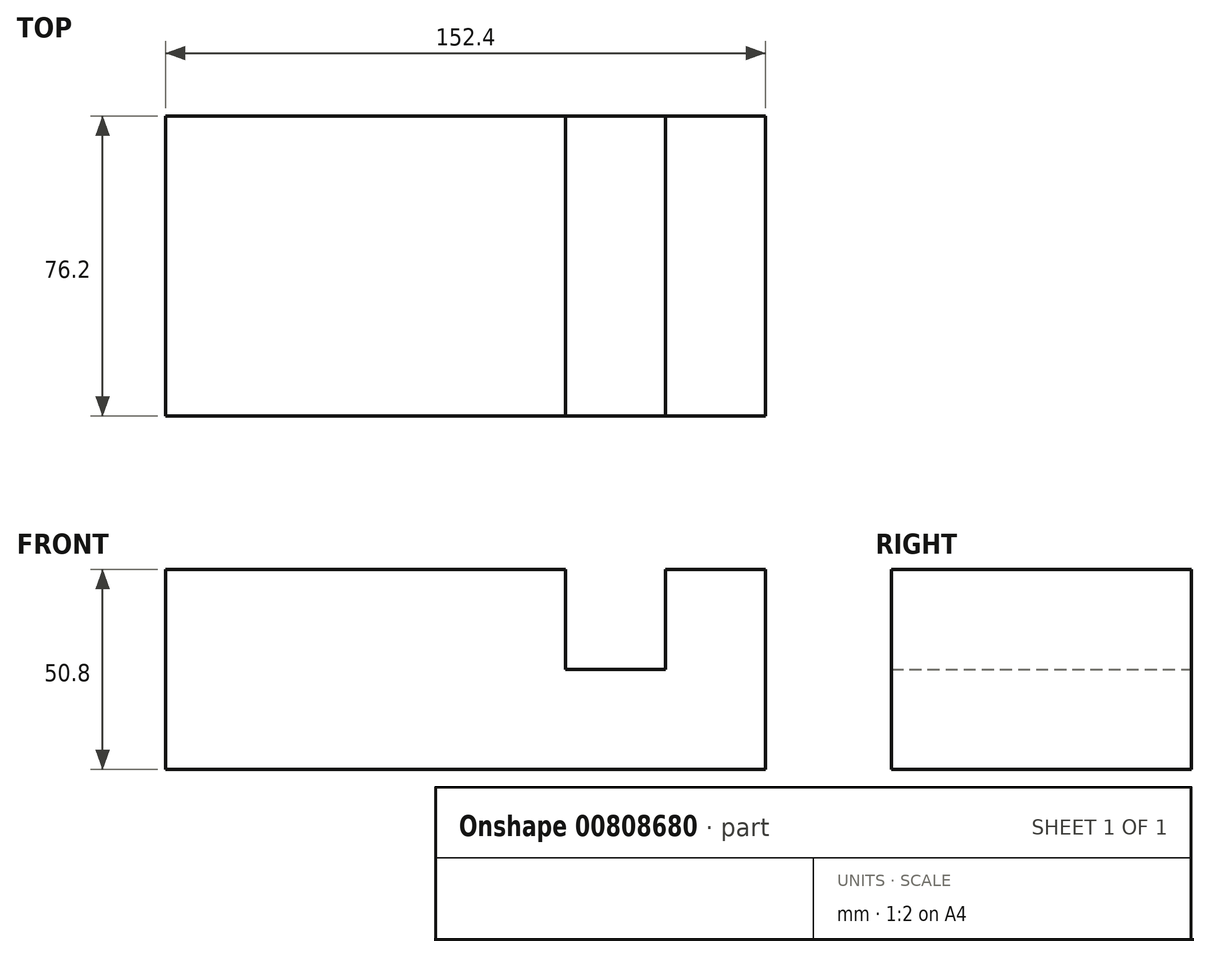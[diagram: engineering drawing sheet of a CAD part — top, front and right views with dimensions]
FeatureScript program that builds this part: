
annotation { "Feature Type Name" : "Feature", "Feature Type Description" : "" }
export const myFeature = defineFeature(function(context is Context, id is Id, definition is map)
    precondition{}
    {
        {
            var Q0;
            Q0=qCreatedBy(makeId("Front.planeOp"),FACE);
            var sketch = newSketch(context, id + "F0", { "sketchPlane" : qUnion([Q0])});
            skLineSegment(sketch, "E0", {"start": v(-75.9, 0) * mm, "end": v(76.5, 0) * mm});
            skLineSegment(sketch, "E1", {"start": v(76.5, 0) * mm, "end": v(76.5, 50.8) * mm});
            skLineSegment(sketch, "E2", {"start": v(76.5, 50.8) * mm, "end": v(51.1, 50.8) * mm});
            skLineSegment(sketch, "E3", {"start": v(51.1, 50.8) * mm, "end": v(51.1, 25.4) * mm});
            skLineSegment(sketch, "E4", {"start": v(51.1, 25.4) * mm, "end": v(25.7, 25.4) * mm});
            skLineSegment(sketch, "E5", {"start": v(25.7, 25.4) * mm, "end": v(25.7, 50.8) * mm});
            skLineSegment(sketch, "E6", {"start": v(25.7, 50.8) * mm, "end": v(-75.9, 50.8) * mm});
            skLineSegment(sketch, "E7", {"start": v(-75.9, 50.8) * mm, "end": v(-75.9, 0) * mm});
            skSolve(sketch);
        }
        {
            var Q0;
            Q0 = qSketchRegion(id + "F0", true);
            extrude(context, id + "F1", {"entities" : qUnion([Q0]), "depth" : 76.2 * mm, "offsetDistance" : 25.4 * mm});
        }
    });
